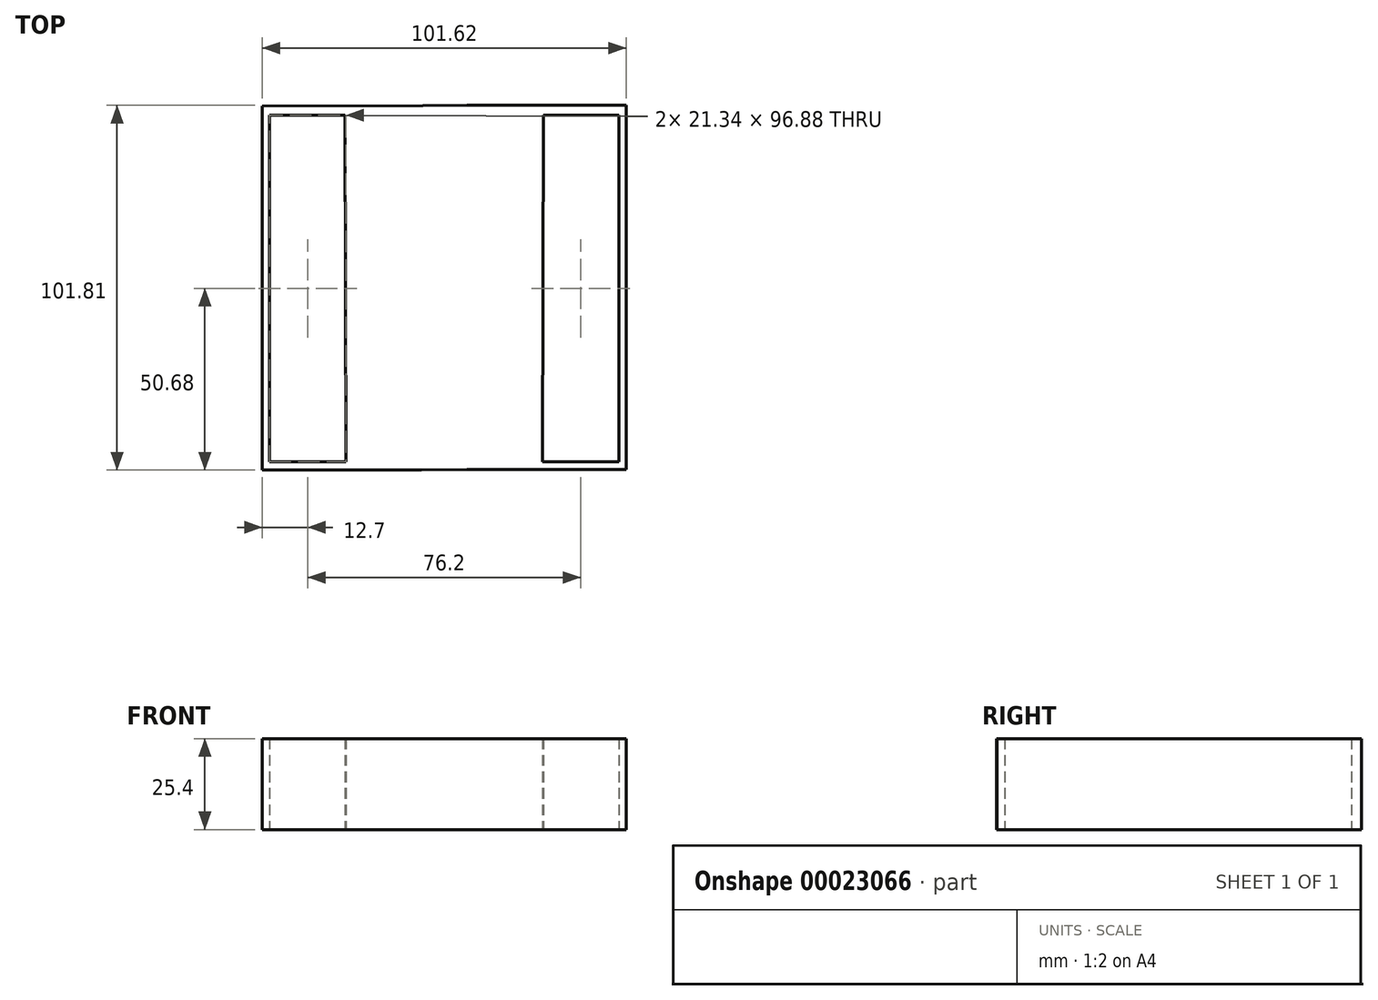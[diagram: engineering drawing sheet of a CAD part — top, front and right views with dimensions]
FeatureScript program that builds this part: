
annotation { "Feature Type Name" : "Feature", "Feature Type Description" : "" }
export const myFeature = defineFeature(function(context is Context, id is Id, definition is map)
    precondition{}
    {
        {
            var Q0;
            Q0=qCreatedBy(makeId("Top.planeOp"),FACE);
            var sketch = newSketch(context, id + "F0", { "sketchPlane" : qUnion([Q0])});
            skLineSegment(sketch, "E0", {"start": v(-50.8, 50.59) * mm, "end": v(-50.8, -51.01) * mm});
            skLineSegment(sketch, "E1", {"start": v(-50.8, -51.01) * mm, "end": v(-41.28, -51.01) * mm});
            skLineSegment(sketch, "E2", {"start": v(50.82, -50.9) * mm, "end": v(50.82, 50.8) * mm});
            skLineSegment(sketch, "E3", {"start": v(50.82, 50.8) * mm, "end": v(39.37, 50.8) * mm});
            skLineSegment(sketch, "E4", {"start": v(-41.28, -51.01) * mm, "end": v(-6.34, -51.01) * mm});
            skLineSegment(sketch, "E5", {"start": v(39.37, 50.8) * mm, "end": v(6.36, 50.8) * mm});
            skLineSegment(sketch, "E6", {"start": v(41.13, -50.9) * mm, "end": v(50.82, -50.9) * mm});
            skLineSegment(sketch, "E7", {"start": v(6.36, -50.9) * mm, "end": v(41.13, -50.9) * mm});
            skPoint(sketch, "E8.end.orphan", {"position": v(0, 50.21) * mm});
            skLineSegment(sketch, "E9", {"start": v(-6.34, 50.68) * mm, "end": v(6.36, 50.8) * mm});
            skLineSegment(sketch, "E10", {"start": v(-6.34, -51.01) * mm, "end": v(6.36, -50.9) * mm});
            skLineSegment(sketch, "E11", {"start": v(-6.34, -51.01) * mm, "end": v(-6.34, 50.68) * mm});
            skLineSegment(sketch, "E12", {"start": v(6.36, 50.8) * mm, "end": v(6.36, -50.9) * mm});
            skLineSegment(sketch, "E13", {"start": v(-25.35, 50.64) * mm, "end": v(-25.35, -51.01) * mm});
            skLineSegment(sketch, "E14", {"start": v(-50.8, 50.59) * mm, "end": v(50.82, 50.8) * mm});
            skLineSegment(sketch, "E15", {"start": v(25.42, 50.75) * mm, "end": v(25.42, -50.9) * mm});
            skLineSegment(sketch, "E16", {"start": v(-48.77, 48.06) * mm, "end": v(-48.77, -48.77) * mm});
            skLineSegment(sketch, "E17", {"start": v(-48.77, 48.06) * mm, "end": v(-27.64, 48.1) * mm});
            skLineSegment(sketch, "E18", {"start": v(-48.77, -48.77) * mm, "end": v(-27.43, -48.77) * mm});
            skLineSegment(sketch, "E19", {"start": v(-27.64, 48.1) * mm, "end": v(-27.43, -48.77) * mm});
            skLineSegment(sketch, "E20.MirrorCS", {"start": v(27.64, 48.1) * mm, "end": v(27.43, -48.77) * mm});
            skLineSegment(sketch, "E21.MirrorCS", {"start": v(48.77, 48.06) * mm, "end": v(48.77, -48.77) * mm});
            skLineSegment(sketch, "E22.MirrorCS", {"start": v(48.77, 48.06) * mm, "end": v(27.64, 48.1) * mm});
            skLineSegment(sketch, "E23.MirrorCS", {"start": v(48.77, -48.77) * mm, "end": v(27.43, -48.77) * mm});
            skLineSegment(sketch, "E24", {"start": v(-7.82, 50.68) * mm, "end": v(-7.61, -51.01) * mm});
            skLineSegment(sketch, "E25.MirrorCS", {"start": v(7.82, 50.68) * mm, "end": v(7.61, -51.01) * mm});
            skSolve(sketch);
        }
        {
            var Q0;
            Q0=qSketchRegion(id+"F0",true);
            extrude(context, id + "F1", {"entities" : qUnion([Q0]), "depth" : 12.7 * mm});
        }
        {
            var Q0;
            Q0 = qSketchRegion(id + "F0", true);
            extrude(context, id + "F2", {"entities" : qUnion([Q0]), "operationType" : NewBodyOperationType.ADD, "depth" : 25.4 * mm});
        }
    });
